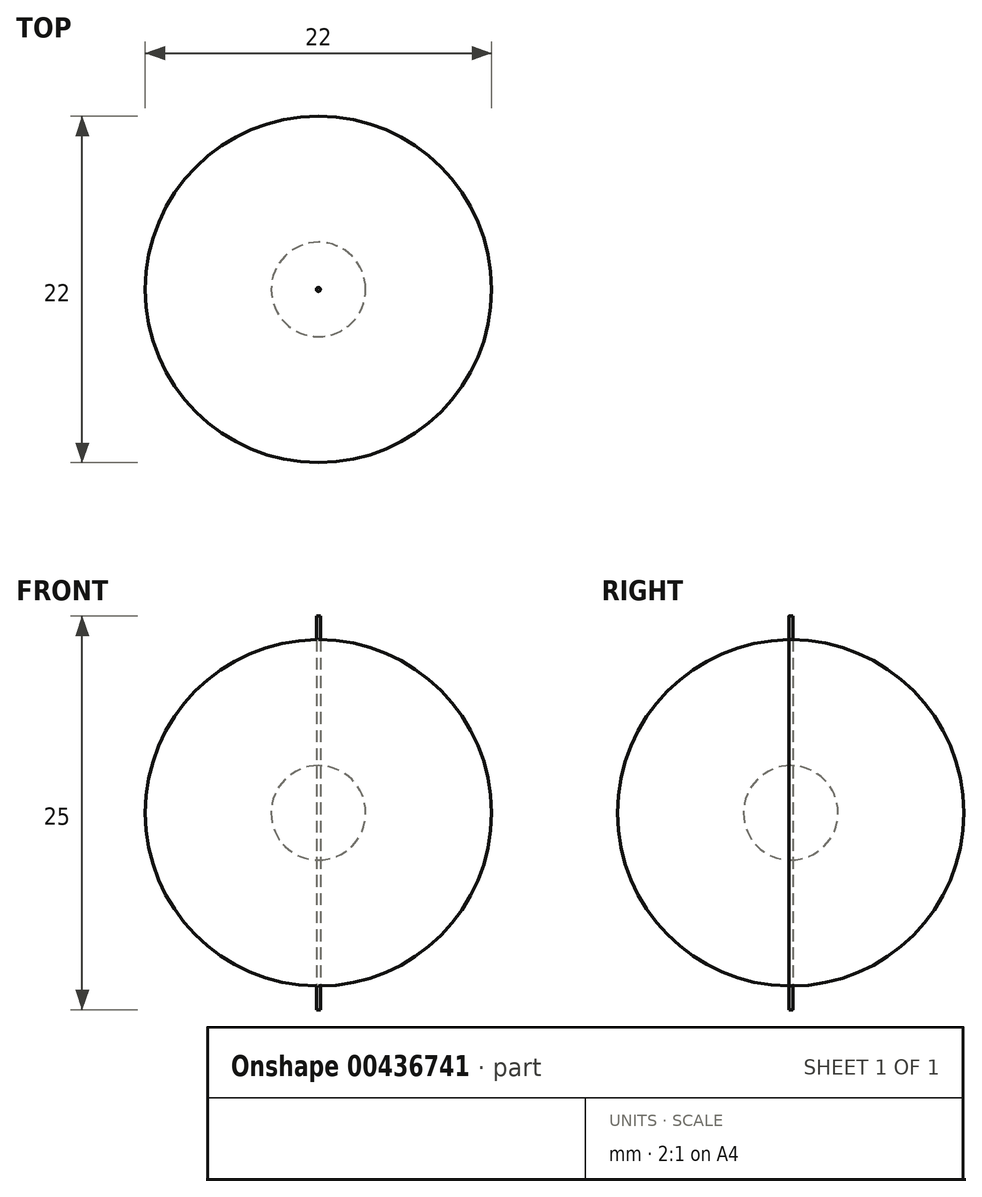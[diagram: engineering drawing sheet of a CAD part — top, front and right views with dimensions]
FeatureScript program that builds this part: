
annotation { "Feature Type Name" : "Feature", "Feature Type Description" : "" }
export const myFeature = defineFeature(function(context is Context, id is Id, definition is map)
    precondition{}
    {
        {
            var Q0;
            Q0=qCreatedBy(makeId("Front.planeOp"),FACE);
            var sketch = newSketch(context, id + "F0", { "sketchPlane" : qUnion([Q0])});
            skLineSegment(sketch, "E0", {"start": v(0, 20.9) * mm, "end": v(0, -19.96) * mm, "construction": true});
            skArc(sketch, "E1", {"start": v(0, 11) * mm, "mid": v(11, 0) * mm, "end": v(0, -11) * mm});
            skLineSegment(sketch, "E2", {"start": v(0, 11) * mm, "end": v(0, -11) * mm});
            skSolve(sketch);
        }
        {
            var Q0;
            Q0 = qSketchRegion(id + "F0", true);
            var Q1;
            Q1=sQuery(id+"F0.wireOp",EDGE,"E0");
            revolve(context, id + "F1", {"entities" : qUnion([Q0]), "axis" : qUnion([Q1]), "revolveType" : RevolveType.FULL});
        }
        {
            var Q0;
            Q0=qCreatedBy(makeId("Front.planeOp"),FACE);
            var sketch = newSketch(context, id + "F2", { "sketchPlane" : qUnion([Q0])});
            skArc(sketch, "E3", {"start": v(0, 3) * mm, "mid": v(3, 0) * mm, "end": v(0, -3) * mm});
            skLineSegment(sketch, "E4", {"start": v(0, -3) * mm, "end": v(0, 3) * mm});
            skLineSegment(sketch, "E5", {"start": v(0, 4.97) * mm, "end": v(0, -4.84) * mm, "construction": true});
            skSolve(sketch);
        }
        {
            var Q0;
            Q0 = qSketchRegion(id + "F2", true);
            var Q1;
            Q1=sQuery(id+"F2.wireOp",EDGE,"E5");
            revolve(context, id + "F3", {"entities" : qUnion([Q0]), "axis" : qUnion([Q1]), "revolveType" : RevolveType.FULL});
        }
        {
            var Q0;
            Q0=qCreatedBy(makeId("Top.planeOp"),FACE);
            var sketch = newSketch(context, id + "F4", { "sketchPlane" : qUnion([Q0])});
            skCircle(sketch, "E6", {"center": v(0, 0) * mm, "radius": 0.12 * mm});
            skSolve(sketch);
        }
        {
            var Q0;
            Q0 = qSketchRegion(id + "F4", true);
            extrude(context, id + "F5", {"entities" : qUnion([Q0]), "depth" : 25 * mm, "offsetDistance" : 25 * mm, "symmetric" : true});
        }
    });
